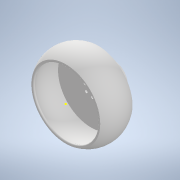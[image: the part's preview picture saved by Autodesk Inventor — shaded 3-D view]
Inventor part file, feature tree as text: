
AUTODESK INVENTOR PART (.ipt)
format: ipt  version: 2020 (Build 240168000, 168)  size: 460,800 bytes
history: native  units: mm
features: sketch x8, extrude x5, other x4, reference x2, sweep x1, shell x1, fillet x1, projected_geometry x1
ambient origin geometry x8: Origin, YZ Plane, XZ Plane, XY Plane, X Axis, Y Axis, Z Axis, Center Point
bodies: Solid1 (feature_tree)
feature tree (23):
  sweep  "Sweep1"
  shell  "Shell1"  Thickness=12.0mm
  extrude  "Extrusion1"  Depth=15.0mm
  extrude  "Extrusion2"  Depth=2.5mm
  extrude  "Extrusion3"  Depth=10.0mm
  fillet  "Fillet1"  Radius=10.0mm
  sketch  "Sketch8"  dims[d16=25.0mm d17=18.0mm]
  extrude  "Extrusion4"  Depth=1.0mm
  extrude  "Extrusion5"  Depth=25.0mm
  sketch  "Sketch1"  dims[d0=75.0mm d1=50.0mm d2=12.0mm]
  sketch  "Sketch2"  dims[d3=30.0mm d4=15.0mm]
  sketch  "Sketch4"  dims[d5=0.0mm d6=0.0mm d7=2.5mm]
  reference  "Reference1"
  reference  "Reference2"
  sketch  "Sketch6"  dims[d8=10.0mm d9=0.0mm d10=5.0mm d11=10.0mm d12=0.0mm]
  sketch  "Sketch7"  dims[d13=4.0mm d14=0.0mm d15=1.0mm]
  projected_geometry  "Projected Loop1"
  sketch  "Sketch9"  dims[d18=14.0mm d19=0.0mm]
  sketch  "Sketch10"  dims[d20=24.92mm d21=40.0mm d22=7.0mm d23=0.0mm]
  other  "<userpath>\Desktop\KangKangBalancing\KangKang.iam"
  other  "KangKang.iam"
  other  "tarot_5008_340kv_assy:1"
  other  "housing0:1"
